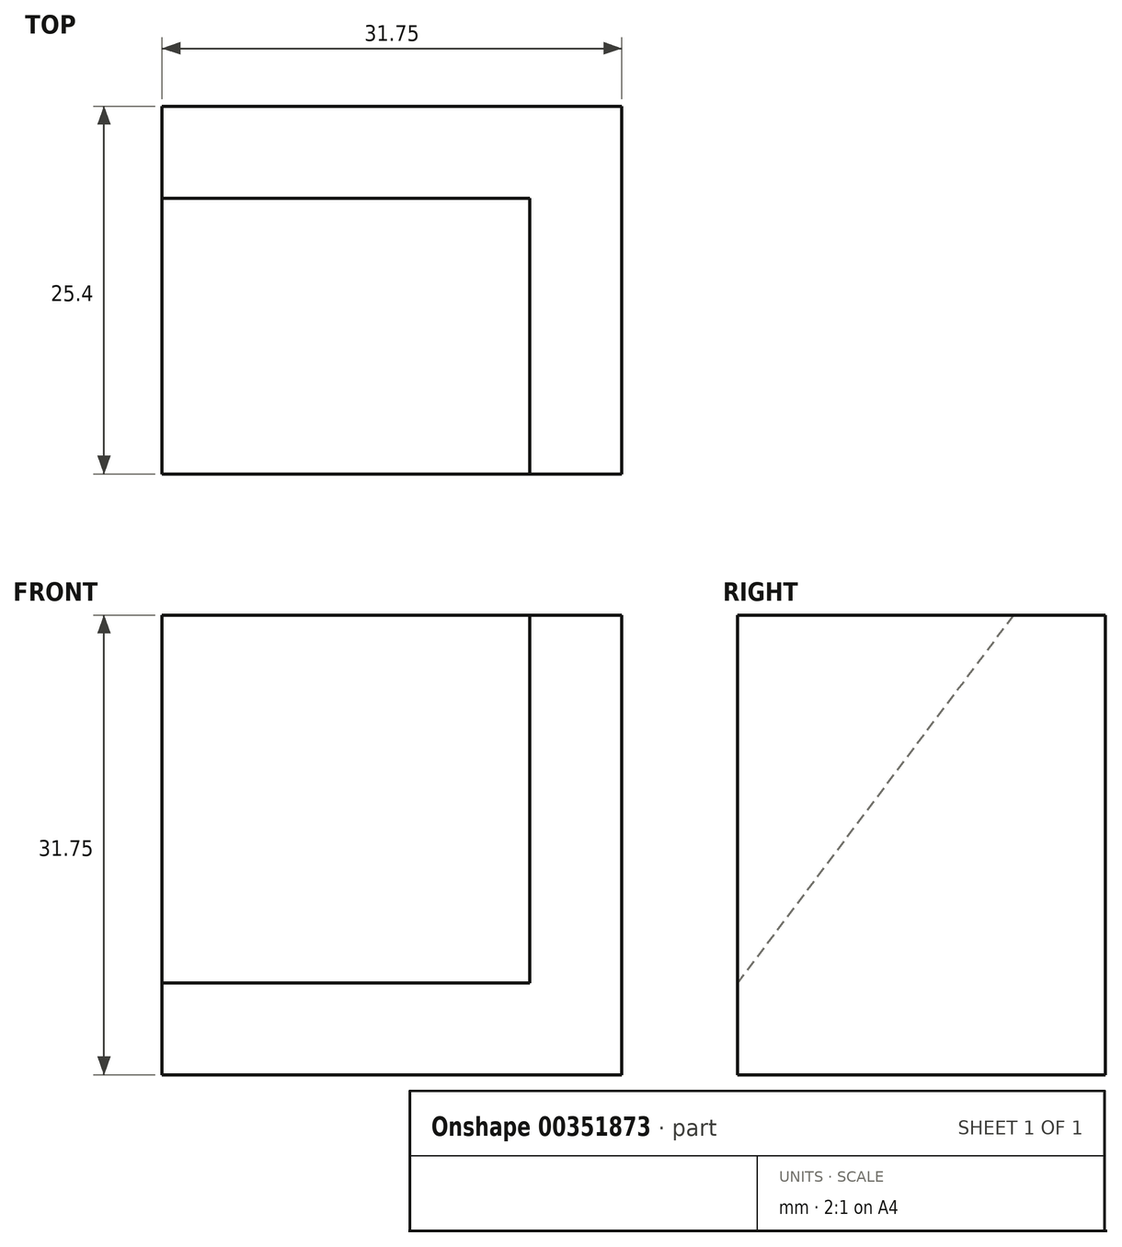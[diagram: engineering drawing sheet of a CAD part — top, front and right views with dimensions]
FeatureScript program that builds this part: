
annotation { "Feature Type Name" : "Feature", "Feature Type Description" : "" }
export const myFeature = defineFeature(function(context is Context, id is Id, definition is map)
    precondition{}
    {
        {
            var Q0;
            Q0=qCreatedBy(makeId("Front.planeOp"),FACE);
            var sketch = newSketch(context, id + "F0", { "sketchPlane" : qUnion([Q0])});
            skLineSegment(sketch, "E0", {"start": v(0, 0) * mm, "end": v(31.75, 0) * mm});
            skLineSegment(sketch, "E1", {"start": v(31.75, 0) * mm, "end": v(31.75, 31.75) * mm});
            skLineSegment(sketch, "E2", {"start": v(31.75, 31.75) * mm, "end": v(0, 31.75) * mm});
            skLineSegment(sketch, "E3", {"start": v(0, 31.75) * mm, "end": v(0, 0) * mm});
            skSolve(sketch);
        }
        {
            var Q0;
            Q0 = qSketchRegion(id + "F0", true);
            extrude(context, id + "F1", {"entities" : qUnion([Q0]), "depth" : 25.4 * mm});
        }
        {
            var Q0;
            Q0=qCreatedBy(makeId("Right.planeOp"),FACE);
            var sketch = newSketch(context, id + "F2", { "sketchPlane" : qUnion([Q0])});
            skLineSegment(sketch, "E4", {"start": v(-6.35, 31.75) * mm, "end": v(-25.4, 6.35) * mm});
            skLineSegment(sketch, "E5", {"start": v(-25.4, 6.35) * mm, "end": v(-25.4, 31.75) * mm});
            skLineSegment(sketch, "E6", {"start": v(-25.4, 31.75) * mm, "end": v(-6.35, 31.75) * mm});
            skSolve(sketch);
        }
        {
            var Q0;
            Q0=makeQuery(id+"F2.imprint","IMPRINT",FACE,{"disambiguationData":[TD([[makeQuery(id+"F2.imprint","IMPRINT",EDGE,{"derivedFrom":sQuery(id+"F2.wireOp",EDGE,"E4")}),-1.0]])]});
            extrude(context, id + "F3", {"entities" : qUnion([Q0]), "operationType" : NewBodyOperationType.REMOVE, "depth" : 25.4 * mm});
        }
    });
